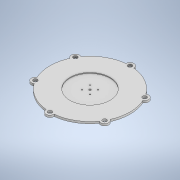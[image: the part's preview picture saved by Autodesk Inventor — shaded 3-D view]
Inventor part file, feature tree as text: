
AUTODESK INVENTOR PART (.ipt)
format: ipt  version: 2022 (Build 260153000, 153)  size: 164,864 bytes
history: native  units: mm
features: extrude x3, sketch x3
ambient origin geometry x8: Origin, YZ Plane, XZ Plane, XY Plane, X Axis, Y Axis, Z Axis, Center Point
bodies: Solid1 (feature_tree)
feature tree (6):
  extrude  "Extrusion1"  Depth=20.0mm
  extrude  "Extrusion2"  Depth=20.0mm
  extrude  "Extrusion3"  Depth=5.0mm
  sketch  "Sketch1"  dims[d0=200.0mm d3=20.0mm]
  sketch  "Sketch2"  dims[d4=20.0mm d5=20.0mm]
  sketch  "Sketch3"  dims[d6=20.0mm d7=20.0mm d8=20.0mm d9=10.0mm d10=10.0mm d11=10.0mm d12=10.0mm d13=10.0mm d14=10.0mm d15=5.0mm d16=0.0mm d17=100.0mm d18=2.0mm d19=0.0mm d20=5.0mm d29=3.0mm d30=3.0mm d31=3.0mm d32=3.0mm d33=5.0mm d34=0.0mm]
